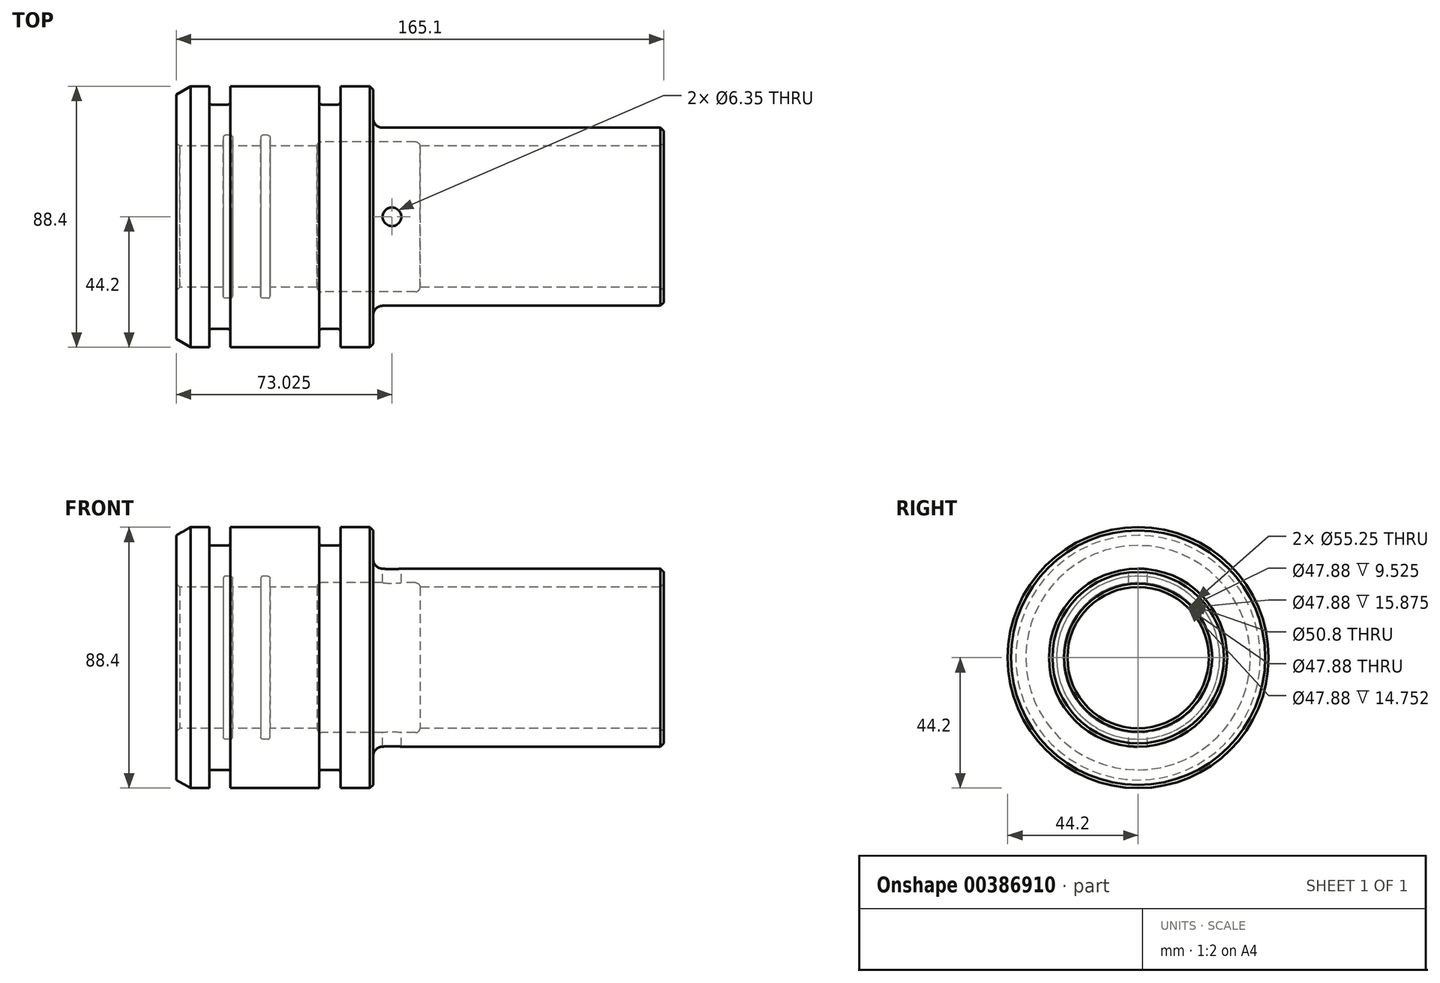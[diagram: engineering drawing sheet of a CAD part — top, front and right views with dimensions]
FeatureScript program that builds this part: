
annotation { "Feature Type Name" : "Feature", "Feature Type Description" : "" }
export const myFeature = defineFeature(function(context is Context, id is Id, definition is map)
    precondition{}
    {
        {
            var Q0;
            Q0=qCreatedBy(makeId("Front.planeOp"),FACE);
            var sketch = newSketch(context, id + "F0", { "sketchPlane" : qUnion([Q0])});
            skLineSegment(sketch, "E0", {"start": v(0, 0) * mm, "end": v(111.33, 0) * mm, "construction": true});
            skLineSegment(sketch, "E1", {"start": v(1.12, 23.94) * mm, "end": v(15.88, 23.94) * mm});
            skLineSegment(sketch, "E2", {"start": v(15.88, 23.94) * mm, "end": v(15.88, 27.62) * mm});
            skLineSegment(sketch, "E3", {"start": v(15.88, 27.62) * mm, "end": v(19.05, 27.62) * mm});
            skLineSegment(sketch, "E4", {"start": v(19.05, 27.62) * mm, "end": v(19.05, 23.94) * mm});
            skLineSegment(sketch, "E5", {"start": v(19.05, 23.94) * mm, "end": v(28.58, 23.94) * mm});
            skLineSegment(sketch, "E6", {"start": v(28.58, 23.94) * mm, "end": v(28.58, 27.62) * mm});
            skLineSegment(sketch, "E7", {"start": v(28.58, 27.62) * mm, "end": v(31.75, 27.62) * mm});
            skLineSegment(sketch, "E8", {"start": v(31.75, 27.62) * mm, "end": v(31.75, 23.94) * mm});
            skLineSegment(sketch, "E9", {"start": v(31.75, 23.94) * mm, "end": v(47.63, 23.94) * mm});
            skLineSegment(sketch, "E10", {"start": v(47.63, 23.94) * mm, "end": v(47.63, 25.4) * mm});
            skLineSegment(sketch, "E11", {"start": v(47.63, 25.4) * mm, "end": v(82.55, 25.4) * mm});
            skLineSegment(sketch, "E12", {"start": v(82.55, 25.4) * mm, "end": v(82.55, 23.94) * mm});
            skLineSegment(sketch, "E13", {"start": v(82.55, 23.94) * mm, "end": v(163.98, 23.94) * mm});
            skLineSegment(sketch, "E14", {"start": v(165.1, 25.06) * mm, "end": v(165.1, 29.04) * mm});
            skLineSegment(sketch, "E15", {"start": v(163.98, 30.16) * mm, "end": v(66.67, 30.16) * mm});
            skLineSegment(sketch, "E16", {"start": v(66.68, 30.16) * mm, "end": v(66.68, 43.07) * mm});
            skLineSegment(sketch, "E17", {"start": v(65.55, 44.2) * mm, "end": v(55.56, 44.2) * mm});
            skLineSegment(sketch, "E18", {"start": v(55.56, 44.2) * mm, "end": v(55.56, 38.02) * mm});
            skLineSegment(sketch, "E19", {"start": v(55.56, 38.02) * mm, "end": v(48.43, 38.02) * mm});
            skLineSegment(sketch, "E20", {"start": v(48.43, 38.02) * mm, "end": v(48.43, 44.2) * mm});
            skLineSegment(sketch, "E21", {"start": v(48.43, 44.2) * mm, "end": v(18.25, 44.2) * mm});
            skLineSegment(sketch, "E22", {"start": v(18.25, 44.2) * mm, "end": v(18.25, 38.02) * mm});
            skLineSegment(sketch, "E23", {"start": v(18.25, 38.02) * mm, "end": v(11.11, 38.02) * mm});
            skLineSegment(sketch, "E24", {"start": v(11.11, 38.02) * mm, "end": v(11.11, 44.2) * mm});
            skLineSegment(sketch, "E25", {"start": v(11.11, 44.2) * mm, "end": v(4.76, 44.2) * mm});
            skLineSegment(sketch, "E26", {"start": v(4.76, 44.2) * mm, "end": v(0, 41.45) * mm});
            skLineSegment(sketch, "E27", {"start": v(0, 41.45) * mm, "end": v(0, 25.06) * mm});
            skLineSegment(sketch, "E28", {"start": v(163.98, 23.94) * mm, "end": v(165.1, 25.06) * mm});
            skLineSegment(sketch, "E29", {"start": v(163.98, 30.16) * mm, "end": v(165.1, 29.04) * mm});
            skLineSegment(sketch, "E30", {"start": v(65.55, 44.2) * mm, "end": v(66.68, 43.07) * mm});
            skLineSegment(sketch, "E31", {"start": v(0, 25.06) * mm, "end": v(1.12, 23.94) * mm});
            skPoint(sketch, "E32.orphan", {"position": v(0, 23.94) * mm});
            skSolve(sketch);
        }
        {
            var Q0;
            Q0 = qSketchRegion(id + "F0", true);
            var Q1;
            Q1=sQuery(id+"F0.wireOp",EDGE,"E0");
            revolve(context, id + "F1", {"entities" : qUnion([Q0]), "axis" : qUnion([Q1]), "revolveType" : RevolveType.FULL});
        }
        {
            var Q0;
            Q0=makeQuery(id+"F1.opRevolve","SWEPT_EDGE",EDGE,{"disambiguationData":[OSD([sQuery(id+"F0.wireOp",EDGE,"E15"),sQuery(id+"F0.wireOp",EDGE,"E16")])]});
            fillet(context, id + "F2", {"entities" : qUnion([Q0]), "radius" : 3.17 * mm, "tangentPropagation" : true, "allowEdgeOverflow" : false});
        }
        {
            var Q0;
            Q0=makeQuery(id+"F1.opRevolve","SWEPT_EDGE",EDGE,{"disambiguationData":[OSD([sQuery(id+"F0.wireOp",EDGE,"E10"),sQuery(id+"F0.wireOp",EDGE,"E11")])]});
            var Q1;
            Q1=makeQuery(id+"F1.opRevolve","SWEPT_EDGE",EDGE,{"disambiguationData":[OSD([sQuery(id+"F0.wireOp",EDGE,"E11"),sQuery(id+"F0.wireOp",EDGE,"E12")])]});
            fillet(context, id + "F3", {"entities" : qUnion([Q0, Q1]), "radius" : 1.59 * mm, "tangentPropagation" : true, "allowEdgeOverflow" : false});
        }
        {
            var Q0;
            Q0=makeQuery(id+"F1.opRevolve","SWEPT_EDGE",EDGE,{"disambiguationData":[OSD([sQuery(id+"F0.wireOp",EDGE,"E22"),sQuery(id+"F0.wireOp",EDGE,"E23")])]});
            var Q1;
            Q1=makeQuery(id+"F1.opRevolve","SWEPT_EDGE",EDGE,{"disambiguationData":[OSD([sQuery(id+"F0.wireOp",EDGE,"E18"),sQuery(id+"F0.wireOp",EDGE,"E19")])]});
            var Q2;
            Q2=makeQuery(id+"F1.opRevolve","SWEPT_EDGE",EDGE,{"disambiguationData":[OSD([sQuery(id+"F0.wireOp",EDGE,"E3"),sQuery(id+"F0.wireOp",EDGE,"E4")])]});
            var Q3;
            Q3=makeQuery(id+"F1.opRevolve","SWEPT_EDGE",EDGE,{"disambiguationData":[OSD([sQuery(id+"F0.wireOp",EDGE,"E7"),sQuery(id+"F0.wireOp",EDGE,"E8")])]});
            var Q4;
            Q4=makeQuery(id+"F1.opRevolve","SWEPT_EDGE",EDGE,{"disambiguationData":[OSD([sQuery(id+"F0.wireOp",EDGE,"E2"),sQuery(id+"F0.wireOp",EDGE,"E3")])]});
            var Q5;
            Q5=makeQuery(id+"F1.opRevolve","SWEPT_EDGE",EDGE,{"disambiguationData":[OSD([sQuery(id+"F0.wireOp",EDGE,"E6"),sQuery(id+"F0.wireOp",EDGE,"E7")])]});
            var Q6;
            Q6=makeQuery(id+"F1.opRevolve","SWEPT_EDGE",EDGE,{"disambiguationData":[OSD([sQuery(id+"F0.wireOp",EDGE,"E23"),sQuery(id+"F0.wireOp",EDGE,"E24")])]});
            var Q7;
            Q7=makeQuery(id+"F1.opRevolve","SWEPT_EDGE",EDGE,{"disambiguationData":[OSD([sQuery(id+"F0.wireOp",EDGE,"E19"),sQuery(id+"F0.wireOp",EDGE,"E20")])]});
            fillet(context, id + "F4", {"entities" : qUnion([Q0, Q1, Q2, Q3, Q4, Q5, Q6, Q7]), "radius" : 0.8 * mm, "tangentPropagation" : true, "allowEdgeOverflow" : false});
        }
        {
            var Q0;
            Q0=qCreatedBy(makeId("Top.planeOp"),FACE);
            var sketch = newSketch(context, id + "F5", { "sketchPlane" : qUnion([Q0])});
            skCircle(sketch, "E33", {"center": v(73.03, 0) * mm, "radius": 3.18 * mm});
            skSolve(sketch);
        }
        {
            var Q0;
            Q0 = qSketchRegion(id + "F5", true);
            extrude(context, id + "F6", {"entities" : qUnion([Q0]), "operationType" : NewBodyOperationType.REMOVE, "oppositeDirection" : true, "depth" : 101.6 * mm, "offsetDistance" : 25.4 * mm, "symmetric" : true});
        }
    });
